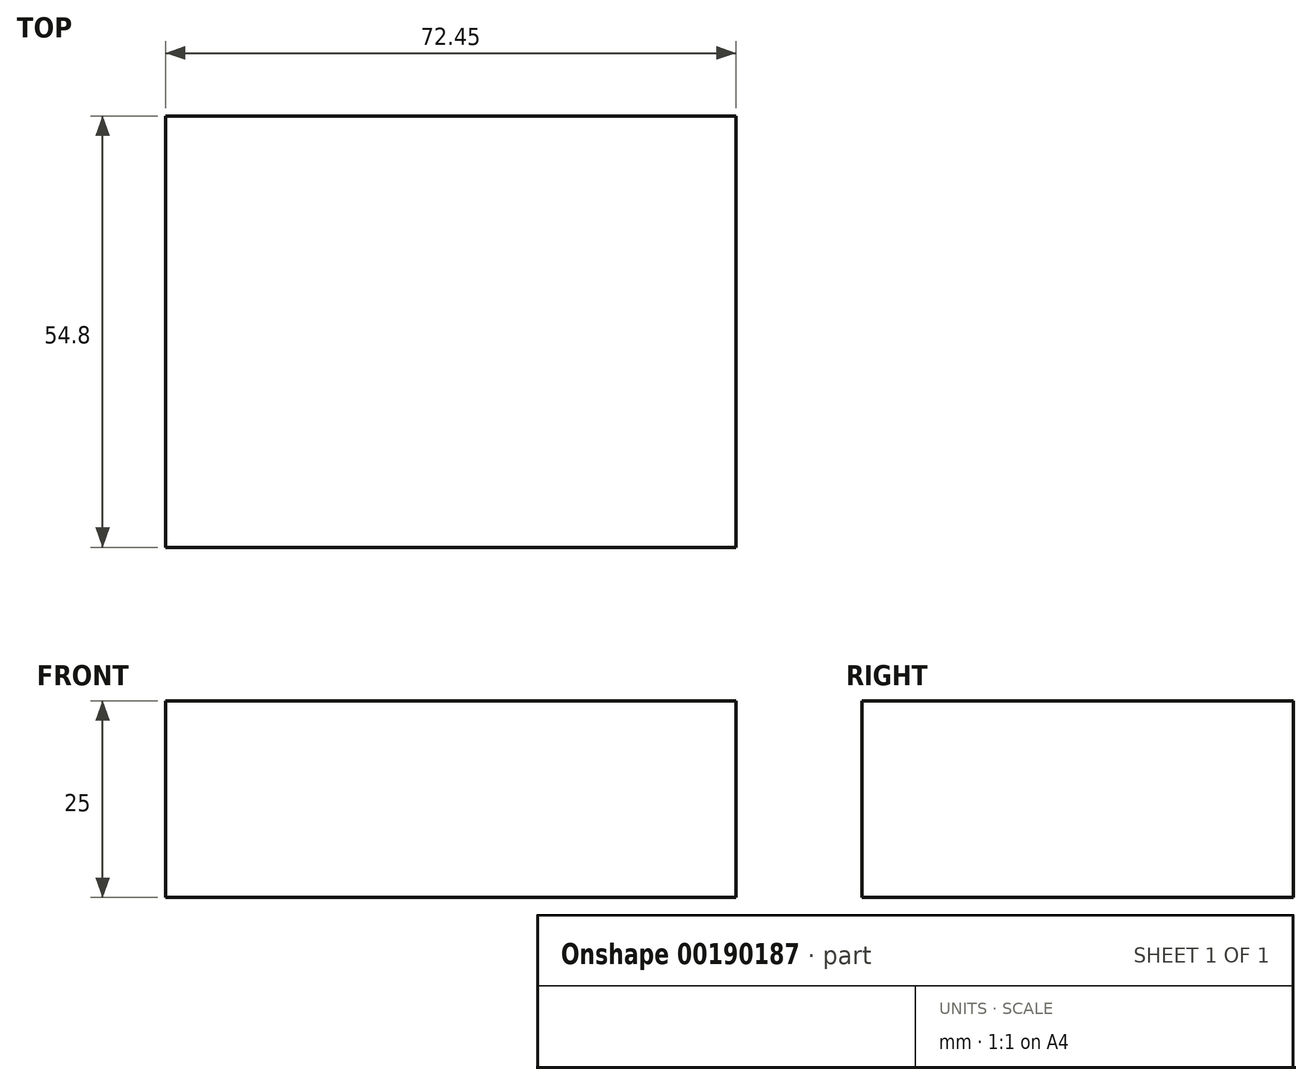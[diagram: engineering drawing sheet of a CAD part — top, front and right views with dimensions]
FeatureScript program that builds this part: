
annotation { "Feature Type Name" : "Feature", "Feature Type Description" : "" }
export const myFeature = defineFeature(function(context is Context, id is Id, definition is map)
    precondition{}
    {
        {
            var Q0;
            Q0=qCreatedBy(makeId("Top.planeOp"),FACE);
            var sketch = newSketch(context, id + "F0", { "sketchPlane" : qUnion([Q0])});
            skLineSegment(sketch, "E0.bottom", {"start": v(-28.33, 16.1) * mm, "end": v(44.12, 16.1) * mm});
            skLineSegment(sketch, "E0.top", {"start": v(-28.33, -38.7) * mm, "end": v(44.12, -38.7) * mm});
            skLineSegment(sketch, "E0.left", {"start": v(-28.33, 16.1) * mm, "end": v(-28.33, -38.7) * mm});
            skLineSegment(sketch, "E0.right", {"start": v(44.12, 16.1) * mm, "end": v(44.12, -38.7) * mm});
            skSolve(sketch);
        }
        {
            var Q0;
            Q0=makeQuery(id+"F0.imprint","IMPRINT",FACE,{"disambiguationData":[TD([[makeQuery(id+"F0.imprint","IMPRINT",EDGE,{"derivedFrom":sQuery(id+"F0.wireOp",EDGE,"E0.bottom")}),-1.0]])]});
            extrude(context, id + "F1", {"entities" : qUnion([Q0]), "depth" : 25 * mm});
        }
    });
